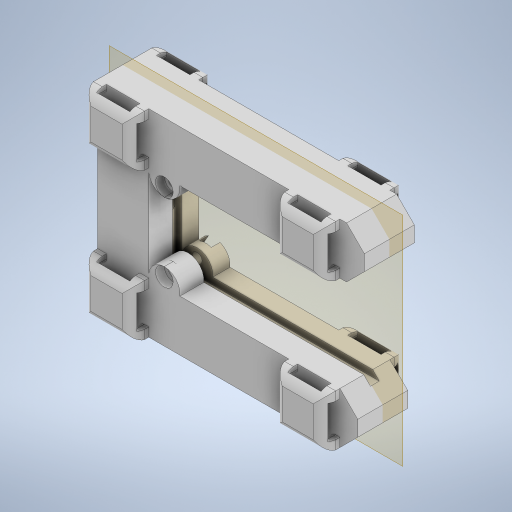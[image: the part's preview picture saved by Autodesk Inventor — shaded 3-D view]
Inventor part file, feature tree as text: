
AUTODESK INVENTOR PART (.ipt)
format: ipt  version: 2024 (Build 280153000, 153)  size: 1,228,288 bytes
history: native  units: mm
features: projected_geometry x18, extrude x14, sketch x14, plane x4, mirror x3, pattern_linear x3, fillet x1, chamfer x1
ambient origin geometry x8: Origin, YZ Plane, XZ Plane, XY Plane, X Axis, Y Axis, Z Axis, Center Point
bodies: Solid1 (feature_tree)
feature tree (58):
  extrude  "Extrusion1"  Depth=10.0mm
  extrude  "Extrusion2"  Depth=1.5mm
  extrude  "Extrusion5"  Depth=1.5mm
  extrude  "Extrusion6"  Depth=3.875mm
  extrude  "Extrusion7"  Depth=10.0mm
  extrude  "Extrusion9"  Depth=2.0mm
  extrude  "Extrusion10"  Depth=5.375mm
  plane  "Work Plane4"
  mirror  "Mirror5"
  extrude  "Extrusion24"  Depth=4.0mm
  extrude  "Extrusion11"  Depth=11.25mm
  extrude  "Extrusion18"  Depth=10.0mm
  pattern_linear  "Rectangular Pattern2"  Spacing1=5.625mm  [1 undecoded]
  pattern_linear  "Rectangular Pattern3"  Spacing1=5.625mm  [1 undecoded]
  plane  "Work Plane3"
  mirror  "Mirror2"
  extrude  "Extrusion19"  Depth=10.0mm
  plane  "Work Plane1"
  extrude  "Extrusion25"  TaperAngle=0.0deg  [1 undecoded]
  fillet  "Fillet2"  Radius=12.0mm
  pattern_linear  "Rectangular Pattern5"  Spacing1=23.5mm  [1 undecoded]
  plane  "Work Plane2"
  mirror  "Mirror6"
  extrude  "Extrusion21"  Depth=48.5mm
  chamfer  "Chamfer1"  [1 undecoded]
  extrude  "Extrusion26"  Depth=2.25mm
  sketch  "Sketch1"  dims[d0=24.5mm d1=10.0mm]
  sketch  "Sketch2"  dims[d2=10.0mm d3=1.5mm]
  projected_geometry  "Projected Loop1"
  sketch  "Sketch5"  dims[d6=10.0mm d7=1.5mm]
  projected_geometry  "Projected Loop6"
  projected_geometry  "Projected Loop7"
  sketch  "Sketch6"  dims[d11=10.0mm d22=3.875mm]
  projected_geometry  "Projected Loop8"
  projected_geometry  "Projected Loop9"
  sketch  "Sketch7"  dims[d23=0.0mm d24=10.0mm]
  projected_geometry  "Projected Loop10"
  projected_geometry  "Projected Loop11"
  sketch  "Sketch9"  dims[d25=10.0mm d26=2.0mm]
  projected_geometry  "Projected Loop13"
  sketch  "Sketch10"  dims[d27=0.0mm d49=5.375mm]
  projected_geometry  "Projected Loop14"
  sketch  "Sketch11"  dims[d50=0.0mm d51=4.0mm]
  projected_geometry  "Projected Loop15"
  sketch  "Sketch18"  dims[d52=4.0mm d53=11.25mm]
  sketch  "Sketch19"  dims[d54=5.625mm d58=10.0mm]
  projected_geometry  "Projected Loop34"
  sketch  "Sketch21"  dims[d59=0.0mm]
  projected_geometry  "Projected Loop36"
  sketch  "Sketch24"  dims[d60=4.0mm]
  projected_geometry  "Projected Loop39"
  projected_geometry  "Projected Loop40"
  sketch  "Sketch25"  dims[d61=4.0mm]
  projected_geometry  "Projected Loop41"
  projected_geometry  "Projected Loop42"
  projected_geometry  "Projected Loop43"
  sketch  "Sketch26"  dims[d62=11.25mm d63=5.625mm d64=5.625mm d67=10.0mm d68=0.0mm d77=12.0mm d78=23.5mm d82=48.5mm d83=0.0mm d84=0.0mm d90=2.25mm d93=11.25mm d94=0.0mm d95=0.0mm d96=0.0mm d146=11.5mm d147=11.5mm d148=0.0mm d150=5.0mm d151=0.0mm d152=2.25mm d153=5.0mm d154=0.0mm d155=1.5mm d156=0.0mm d157=7.0mm d158=1.5mm d159=1.5mm d160=0.0mm d161=12.0mm d162=0.0mm d174=11.5mm d176=0.0mm d177=11.5mm d181=20.0mm d183=33.0mm d184=20.0mm d186=43.0mm d193=4.0mm d194=2.0mm d195=0.0mm d210=1.5mm d211=10.0mm d212=10.0mm d213=44.5mm d214=22.25mm d215=3.5mm d216=5.5mm d217=5.0mm d218=0.0mm d219=0.0mm d220=7.0mm d221=0.0mm d222=1.5mm d223=2.25mm d224=0.0mm d225=7.0mm d227=2.0mm d228=0.0mm d230=2.25mm d231=1.5mm d232=0.0mm d233=6.155119mm d234=0.0mm d235=2.0mm d236=3.5mm d237=3.5mm d238=2.0mm d239=0.0mm d240=2.0mm d241=2.25mm d242=0.0mm d243=7.0mm d244=3.5mm d245=3.5mm d246=1.5mm d247=12.0mm d248=0.0mm d249=1.0mm d250=20.0mm d252=33.0mm d253=20.0mm d255=43.0mm d256=0.0mm d257=4.0mm d258=4.0mm d259=2.0mm d260=45.0deg d262=4.0mm d263=4.0mm d264=90.0deg d265=90.0deg d266=2.0mm d267=0.0mm d202=0.5mm d203=0.872665mm d204=0.5mm d205=0.872665mm d206=0.872665mm d207=0.5mm d208=0.872665mm]
  projected_geometry  "Projected Loop44"
note: 5 required parameter values undecoded (feature->parameter linkage not recoverable at this tier; creation-order binding heuristic only, values carry confidence <= 0.55)
